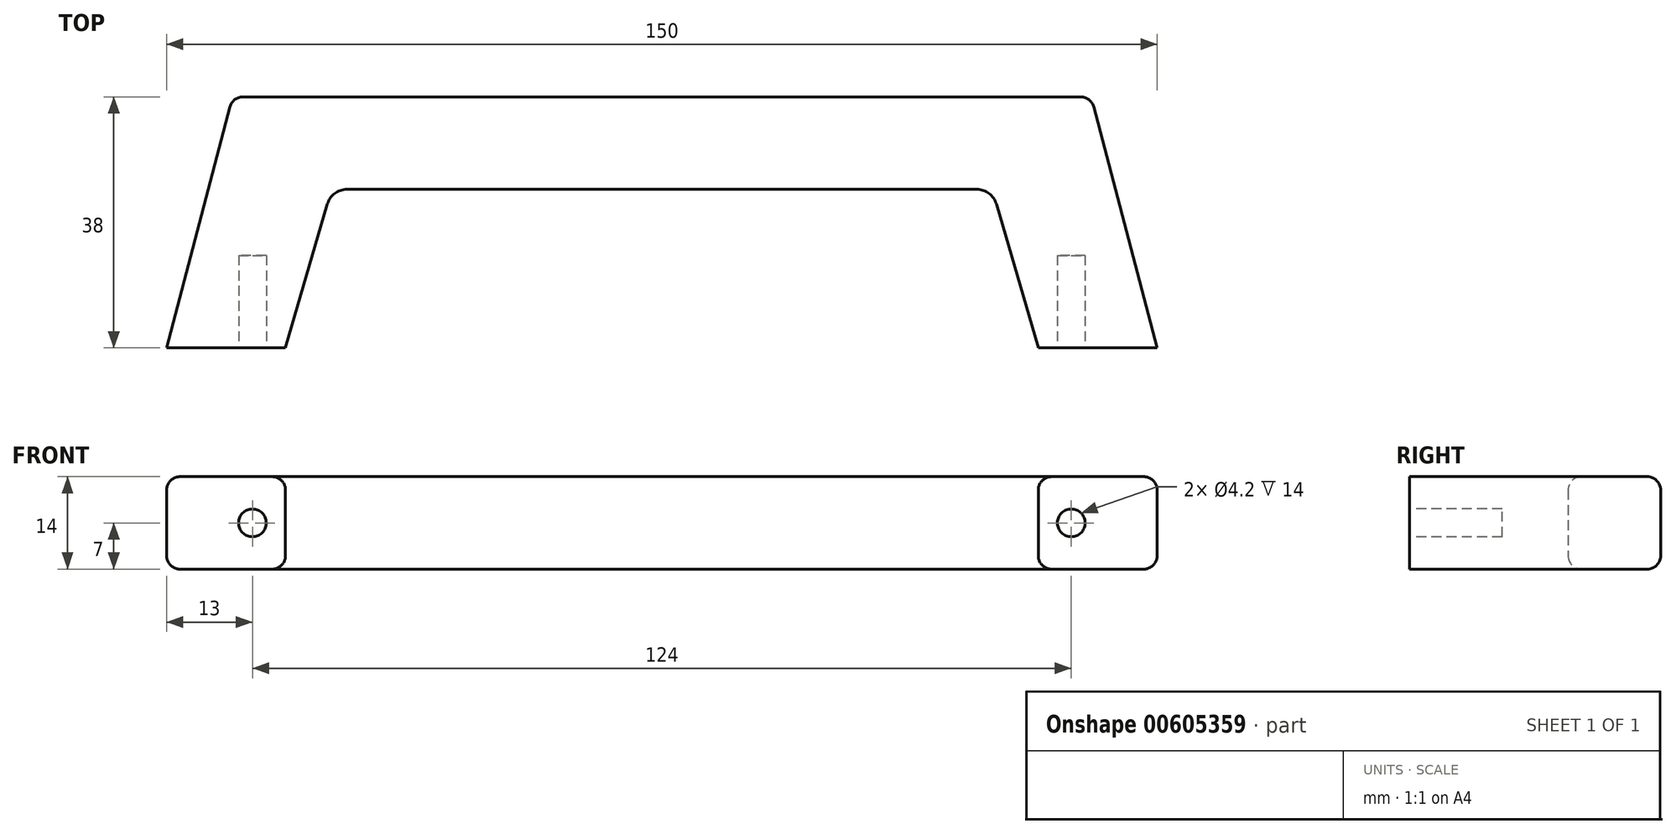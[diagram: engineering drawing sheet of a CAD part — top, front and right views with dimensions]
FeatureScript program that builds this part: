
annotation { "Feature Type Name" : "Feature", "Feature Type Description" : "" }
export const myFeature = defineFeature(function(context is Context, id is Id, definition is map)
    precondition{}
    {
        {
            var Q0;
            Q0=qCreatedBy(makeId("Top.planeOp"),FACE);
            var sketch = newSketch(context, id + "F0", { "sketchPlane" : qUnion([Q0])});
            skPoint(sketch, "E0.middle", {"position": v(0, 0) * mm});
            skLineSegment(sketch, "E1", {"start": v(-75, -19.5) * mm, "end": v(-65, 18.5) * mm});
            skLineSegment(sketch, "E2", {"start": v(-65, 18.5) * mm, "end": v(0, 18.5) * mm});
            skLineSegment(sketch, "E3", {"start": v(-75, -19.5) * mm, "end": v(-57, -19.5) * mm});
            skLineSegment(sketch, "E4", {"start": v(-50, 4.5) * mm, "end": v(0, 4.5) * mm});
            skLineSegment(sketch, "E5", {"start": v(-57, -19.5) * mm, "end": v(-50, 4.5) * mm});
            skPoint(sketch, "E6.orphan", {"position": v(0, 38.21) * mm});
            skPoint(sketch, "E0.right.end.orphan", {"position": v(75, -19.5) * mm});
            skPoint(sketch, "E0.right.start.orphan", {"position": v(75, 19.5) * mm});
            skLineSegment(sketch, "E7.MirrorCS", {"start": v(65, 18.5) * mm, "end": v(0, 18.5) * mm});
            skLineSegment(sketch, "E8.MirrorCS", {"start": v(50, 4.5) * mm, "end": v(0, 4.5) * mm});
            skLineSegment(sketch, "E9.MirrorCS", {"start": v(57, -19.5) * mm, "end": v(50, 4.5) * mm});
            skLineSegment(sketch, "E10.MirrorCS", {"start": v(75, -19.5) * mm, "end": v(65, 18.5) * mm});
            skLineSegment(sketch, "E11.MirrorCS", {"start": v(75, -19.5) * mm, "end": v(57, -19.5) * mm});
            skSolve(sketch);
        }
        {
            var Q0;
            Q0=makeQuery(id+"F0.imprint","IMPRINT",FACE,{"disambiguationData":[TD([[makeQuery(id+"F0.imprint","IMPRINT",EDGE,{"derivedFrom":sQuery(id+"F0.wireOp",EDGE,"E1")}),-1.0]])]});
            extrude(context, id + "F1", {"entities" : qUnion([Q0]), "depth" : 14 * mm, "offsetDistance" : 25 * mm});
        }
        {
            var Q0;
            Q0=makeQuery(id+"F1.opExtrude","SWEPT_FACE",FACE,{"disambiguationData":[OSD([sQuery(id+"F0.wireOp",EDGE,"E3")])]});
            var sketch = newSketch(context, id + "F2", { "sketchPlane" : qUnion([Q0])});
            skCircle(sketch, "E12", {"center": v(-62, 7) * mm, "radius": 2.1 * mm});
            skPoint(sketch, "E12.centerSnap0", {"position": v(-57, 7) * mm});
            skCircle(sketch, "E13.MirrorC", {"center": v(62, 7) * mm, "radius": 2.1 * mm});
            skSolve(sketch);
        }
        {
            var Q0;
            Q0 = qSketchRegion(id + "F2", true);
            extrude(context, id + "F3", {"entities" : qUnion([Q0]), "operationType" : NewBodyOperationType.REMOVE, "oppositeDirection" : true, "depth" : 14 * mm, "offsetDistance" : 25 * mm});
        }
        {
            var Q0;
            Q0=makeQuery(id+"F1.opExtrude","SWEPT_EDGE",EDGE,{"disambiguationData":[OSD([sQuery(id+"F0.wireOp",EDGE,"E7.MirrorCS"),sQuery(id+"F0.wireOp",EDGE,"E10.MirrorCS")])]});
            var Q1;
            Q1=makeQuery(id+"F1.opExtrude","SWEPT_EDGE",EDGE,{"disambiguationData":[OSD([sQuery(id+"F0.wireOp",EDGE,"E1"),sQuery(id+"F0.wireOp",EDGE,"E2")])]});
            fillet(context, id + "F4", {"entities" : qUnion([Q0, Q1]), "radius" : 2 * mm, "tangentPropagation" : true, "allowEdgeOverflow" : false});
        }
        {
            var Q0;
            Q0=makeQuery(id+"F1.opExtrude","SWEPT_EDGE",EDGE,{"disambiguationData":[OSD([sQuery(id+"F0.wireOp",EDGE,"E8.MirrorCS"),sQuery(id+"F0.wireOp",EDGE,"E9.MirrorCS")])]});
            var Q1;
            Q1=makeQuery(id+"F1.opExtrude","SWEPT_EDGE",EDGE,{"disambiguationData":[OSD([sQuery(id+"F0.wireOp",EDGE,"E4"),sQuery(id+"F0.wireOp",EDGE,"E5")])]});
            fillet(context, id + "F5", {"entities" : qUnion([Q0, Q1]), "radius" : 3.1 * mm, "tangentPropagation" : true, "allowEdgeOverflow" : false});
        }
        {
            var Q0;
            Q0=makeQuery(id+"F1.opExtrude","CAP_EDGE",EDGE,{"disambiguationData":[OSD([sQuery(id+"F0.wireOp",EDGE,"E2"),sQuery(id+"F0.wireOp",EDGE,"E7.MirrorCS")])],"isStart":true});
            var Q1;
            {var subQ0=sQuery(id+"F0.wireOp",EDGE,"E2");var subQ1=sQuery(id+"F0.wireOp",EDGE,"E1");Q1=makeQuery(id+"F4.opFillet","BLEND_EDGE",EDGE,{"blendedFrom":[makeQuery(id+"F1.opExtrude","SWEPT_EDGE",EDGE,{"disambiguationData":[OSD([subQ1,subQ0])]}),makeQuery(id+"F1.opExtrude","CAP_FACE",FACE,{"disambiguationData":[OSD([subQ1,subQ0,sQuery(id+"F0.wireOp",EDGE,"E3"),sQuery(id+"F0.wireOp",EDGE,"E4"),sQuery(id+"F0.wireOp",EDGE,"E5"),sQuery(id+"F0.wireOp",EDGE,"E7.MirrorCS"),sQuery(id+"F0.wireOp",EDGE,"E8.MirrorCS"),sQuery(id+"F0.wireOp",EDGE,"E9.MirrorCS"),sQuery(id+"F0.wireOp",EDGE,"E10.MirrorCS"),sQuery(id+"F0.wireOp",EDGE,"E11.MirrorCS")])],"isStart":true})],"blendedInto":[makeQuery(id+"F1.opExtrude","CAP_FACE",FACE,{"disambiguationData":[OSD([subQ1,subQ0,sQuery(id+"F0.wireOp",EDGE,"E3"),sQuery(id+"F0.wireOp",EDGE,"E4"),sQuery(id+"F0.wireOp",EDGE,"E5"),sQuery(id+"F0.wireOp",EDGE,"E7.MirrorCS"),sQuery(id+"F0.wireOp",EDGE,"E8.MirrorCS"),sQuery(id+"F0.wireOp",EDGE,"E9.MirrorCS"),sQuery(id+"F0.wireOp",EDGE,"E10.MirrorCS"),sQuery(id+"F0.wireOp",EDGE,"E11.MirrorCS")])],"isStart":true})]});}
            var Q2;
            Q2=makeQuery(id+"F1.opExtrude","CAP_EDGE",EDGE,{"disambiguationData":[OSD([sQuery(id+"F0.wireOp",EDGE,"E1")])],"isStart":true});
            var Q3;
            {var subQ0=sQuery(id+"F0.wireOp",EDGE,"E10.MirrorCS");var subQ1=sQuery(id+"F0.wireOp",EDGE,"E7.MirrorCS");Q3=makeQuery(id+"F4.opFillet","BLEND_EDGE",EDGE,{"blendedFrom":[makeQuery(id+"F1.opExtrude","SWEPT_EDGE",EDGE,{"disambiguationData":[OSD([subQ1,subQ0])]}),makeQuery(id+"F1.opExtrude","CAP_FACE",FACE,{"disambiguationData":[OSD([sQuery(id+"F0.wireOp",EDGE,"E1"),sQuery(id+"F0.wireOp",EDGE,"E2"),sQuery(id+"F0.wireOp",EDGE,"E3"),sQuery(id+"F0.wireOp",EDGE,"E4"),sQuery(id+"F0.wireOp",EDGE,"E5"),subQ1,sQuery(id+"F0.wireOp",EDGE,"E8.MirrorCS"),sQuery(id+"F0.wireOp",EDGE,"E9.MirrorCS"),subQ0,sQuery(id+"F0.wireOp",EDGE,"E11.MirrorCS")])],"isStart":true})],"blendedInto":[makeQuery(id+"F1.opExtrude","CAP_FACE",FACE,{"disambiguationData":[OSD([sQuery(id+"F0.wireOp",EDGE,"E1"),sQuery(id+"F0.wireOp",EDGE,"E2"),sQuery(id+"F0.wireOp",EDGE,"E3"),sQuery(id+"F0.wireOp",EDGE,"E4"),sQuery(id+"F0.wireOp",EDGE,"E5"),subQ1,sQuery(id+"F0.wireOp",EDGE,"E8.MirrorCS"),sQuery(id+"F0.wireOp",EDGE,"E9.MirrorCS"),subQ0,sQuery(id+"F0.wireOp",EDGE,"E11.MirrorCS")])],"isStart":true})]});}
            var Q4;
            Q4=makeQuery(id+"F1.opExtrude","CAP_EDGE",EDGE,{"disambiguationData":[OSD([sQuery(id+"F0.wireOp",EDGE,"E10.MirrorCS")])],"isStart":true});
            var Q5;
            Q5=makeQuery(id+"F1.opExtrude","CAP_EDGE",EDGE,{"disambiguationData":[OSD([sQuery(id+"F0.wireOp",EDGE,"E9.MirrorCS")])],"isStart":true});
            var Q6;
            {var subQ0=sQuery(id+"F0.wireOp",EDGE,"E9.MirrorCS");var subQ1=sQuery(id+"F0.wireOp",EDGE,"E8.MirrorCS");Q6=makeQuery(id+"F5.opFillet","BLEND_EDGE",EDGE,{"blendedFrom":[makeQuery(id+"F1.opExtrude","SWEPT_EDGE",EDGE,{"disambiguationData":[OSD([subQ1,subQ0])]}),makeQuery(id+"F1.opExtrude","CAP_FACE",FACE,{"disambiguationData":[OSD([sQuery(id+"F0.wireOp",EDGE,"E1"),sQuery(id+"F0.wireOp",EDGE,"E2"),sQuery(id+"F0.wireOp",EDGE,"E3"),sQuery(id+"F0.wireOp",EDGE,"E4"),sQuery(id+"F0.wireOp",EDGE,"E5"),sQuery(id+"F0.wireOp",EDGE,"E7.MirrorCS"),subQ1,subQ0,sQuery(id+"F0.wireOp",EDGE,"E10.MirrorCS"),sQuery(id+"F0.wireOp",EDGE,"E11.MirrorCS")])],"isStart":true})],"blendedInto":[makeQuery(id+"F1.opExtrude","CAP_FACE",FACE,{"disambiguationData":[OSD([sQuery(id+"F0.wireOp",EDGE,"E1"),sQuery(id+"F0.wireOp",EDGE,"E2"),sQuery(id+"F0.wireOp",EDGE,"E3"),sQuery(id+"F0.wireOp",EDGE,"E4"),sQuery(id+"F0.wireOp",EDGE,"E5"),sQuery(id+"F0.wireOp",EDGE,"E7.MirrorCS"),subQ1,subQ0,sQuery(id+"F0.wireOp",EDGE,"E10.MirrorCS"),sQuery(id+"F0.wireOp",EDGE,"E11.MirrorCS")])],"isStart":true})]});}
            var Q7;
            Q7=makeQuery(id+"F1.opExtrude","CAP_EDGE",EDGE,{"disambiguationData":[OSD([sQuery(id+"F0.wireOp",EDGE,"E4"),sQuery(id+"F0.wireOp",EDGE,"E8.MirrorCS")])],"isStart":true});
            var Q8;
            {var subQ0=sQuery(id+"F0.wireOp",EDGE,"E5");var subQ1=sQuery(id+"F0.wireOp",EDGE,"E4");Q8=makeQuery(id+"F5.opFillet","BLEND_EDGE",EDGE,{"blendedFrom":[makeQuery(id+"F1.opExtrude","SWEPT_EDGE",EDGE,{"disambiguationData":[OSD([subQ1,subQ0])]}),makeQuery(id+"F1.opExtrude","CAP_FACE",FACE,{"disambiguationData":[OSD([sQuery(id+"F0.wireOp",EDGE,"E1"),sQuery(id+"F0.wireOp",EDGE,"E2"),sQuery(id+"F0.wireOp",EDGE,"E3"),subQ1,subQ0,sQuery(id+"F0.wireOp",EDGE,"E7.MirrorCS"),sQuery(id+"F0.wireOp",EDGE,"E8.MirrorCS"),sQuery(id+"F0.wireOp",EDGE,"E9.MirrorCS"),sQuery(id+"F0.wireOp",EDGE,"E10.MirrorCS"),sQuery(id+"F0.wireOp",EDGE,"E11.MirrorCS")])],"isStart":true})],"blendedInto":[makeQuery(id+"F1.opExtrude","CAP_FACE",FACE,{"disambiguationData":[OSD([sQuery(id+"F0.wireOp",EDGE,"E1"),sQuery(id+"F0.wireOp",EDGE,"E2"),sQuery(id+"F0.wireOp",EDGE,"E3"),subQ1,subQ0,sQuery(id+"F0.wireOp",EDGE,"E7.MirrorCS"),sQuery(id+"F0.wireOp",EDGE,"E8.MirrorCS"),sQuery(id+"F0.wireOp",EDGE,"E9.MirrorCS"),sQuery(id+"F0.wireOp",EDGE,"E10.MirrorCS"),sQuery(id+"F0.wireOp",EDGE,"E11.MirrorCS")])],"isStart":true})]});}
            var Q9;
            Q9=makeQuery(id+"F1.opExtrude","CAP_EDGE",EDGE,{"disambiguationData":[OSD([sQuery(id+"F0.wireOp",EDGE,"E5")])],"isStart":true});
            var Q10;
            Q10=makeQuery(id+"F1.opExtrude","CAP_EDGE",EDGE,{"disambiguationData":[OSD([sQuery(id+"F0.wireOp",EDGE,"E1")])],"isStart":false});
            var Q11;
            {var subQ0=sQuery(id+"F0.wireOp",EDGE,"E2");var subQ1=sQuery(id+"F0.wireOp",EDGE,"E1");Q11=makeQuery(id+"F4.opFillet","BLEND_EDGE",EDGE,{"blendedFrom":[makeQuery(id+"F1.opExtrude","SWEPT_EDGE",EDGE,{"disambiguationData":[OSD([subQ1,subQ0])]}),makeQuery(id+"F1.opExtrude","CAP_FACE",FACE,{"disambiguationData":[OSD([subQ1,subQ0,sQuery(id+"F0.wireOp",EDGE,"E3"),sQuery(id+"F0.wireOp",EDGE,"E4"),sQuery(id+"F0.wireOp",EDGE,"E5"),sQuery(id+"F0.wireOp",EDGE,"E7.MirrorCS"),sQuery(id+"F0.wireOp",EDGE,"E8.MirrorCS"),sQuery(id+"F0.wireOp",EDGE,"E9.MirrorCS"),sQuery(id+"F0.wireOp",EDGE,"E10.MirrorCS"),sQuery(id+"F0.wireOp",EDGE,"E11.MirrorCS")])],"isStart":false})],"blendedInto":[makeQuery(id+"F1.opExtrude","CAP_FACE",FACE,{"disambiguationData":[OSD([subQ1,subQ0,sQuery(id+"F0.wireOp",EDGE,"E3"),sQuery(id+"F0.wireOp",EDGE,"E4"),sQuery(id+"F0.wireOp",EDGE,"E5"),sQuery(id+"F0.wireOp",EDGE,"E7.MirrorCS"),sQuery(id+"F0.wireOp",EDGE,"E8.MirrorCS"),sQuery(id+"F0.wireOp",EDGE,"E9.MirrorCS"),sQuery(id+"F0.wireOp",EDGE,"E10.MirrorCS"),sQuery(id+"F0.wireOp",EDGE,"E11.MirrorCS")])],"isStart":false})]});}
            var Q12;
            Q12=makeQuery(id+"F1.opExtrude","CAP_EDGE",EDGE,{"disambiguationData":[OSD([sQuery(id+"F0.wireOp",EDGE,"E2"),sQuery(id+"F0.wireOp",EDGE,"E7.MirrorCS")])],"isStart":false});
            var Q13;
            {var subQ0=sQuery(id+"F0.wireOp",EDGE,"E10.MirrorCS");var subQ1=sQuery(id+"F0.wireOp",EDGE,"E7.MirrorCS");Q13=makeQuery(id+"F4.opFillet","BLEND_EDGE",EDGE,{"blendedFrom":[makeQuery(id+"F1.opExtrude","SWEPT_EDGE",EDGE,{"disambiguationData":[OSD([subQ1,subQ0])]}),makeQuery(id+"F1.opExtrude","CAP_FACE",FACE,{"disambiguationData":[OSD([sQuery(id+"F0.wireOp",EDGE,"E1"),sQuery(id+"F0.wireOp",EDGE,"E2"),sQuery(id+"F0.wireOp",EDGE,"E3"),sQuery(id+"F0.wireOp",EDGE,"E4"),sQuery(id+"F0.wireOp",EDGE,"E5"),subQ1,sQuery(id+"F0.wireOp",EDGE,"E8.MirrorCS"),sQuery(id+"F0.wireOp",EDGE,"E9.MirrorCS"),subQ0,sQuery(id+"F0.wireOp",EDGE,"E11.MirrorCS")])],"isStart":false})],"blendedInto":[makeQuery(id+"F1.opExtrude","CAP_FACE",FACE,{"disambiguationData":[OSD([sQuery(id+"F0.wireOp",EDGE,"E1"),sQuery(id+"F0.wireOp",EDGE,"E2"),sQuery(id+"F0.wireOp",EDGE,"E3"),sQuery(id+"F0.wireOp",EDGE,"E4"),sQuery(id+"F0.wireOp",EDGE,"E5"),subQ1,sQuery(id+"F0.wireOp",EDGE,"E8.MirrorCS"),sQuery(id+"F0.wireOp",EDGE,"E9.MirrorCS"),subQ0,sQuery(id+"F0.wireOp",EDGE,"E11.MirrorCS")])],"isStart":false})]});}
            var Q14;
            Q14=makeQuery(id+"F1.opExtrude","CAP_EDGE",EDGE,{"disambiguationData":[OSD([sQuery(id+"F0.wireOp",EDGE,"E10.MirrorCS")])],"isStart":false});
            var Q15;
            {var subQ0=sQuery(id+"F0.wireOp",EDGE,"E9.MirrorCS");var subQ1=sQuery(id+"F0.wireOp",EDGE,"E8.MirrorCS");Q15=makeQuery(id+"F5.opFillet","BLEND_EDGE",EDGE,{"blendedFrom":[makeQuery(id+"F1.opExtrude","SWEPT_EDGE",EDGE,{"disambiguationData":[OSD([subQ1,subQ0])]}),makeQuery(id+"F1.opExtrude","CAP_FACE",FACE,{"disambiguationData":[OSD([sQuery(id+"F0.wireOp",EDGE,"E1"),sQuery(id+"F0.wireOp",EDGE,"E2"),sQuery(id+"F0.wireOp",EDGE,"E3"),sQuery(id+"F0.wireOp",EDGE,"E4"),sQuery(id+"F0.wireOp",EDGE,"E5"),sQuery(id+"F0.wireOp",EDGE,"E7.MirrorCS"),subQ1,subQ0,sQuery(id+"F0.wireOp",EDGE,"E10.MirrorCS"),sQuery(id+"F0.wireOp",EDGE,"E11.MirrorCS")])],"isStart":false})],"blendedInto":[makeQuery(id+"F1.opExtrude","CAP_FACE",FACE,{"disambiguationData":[OSD([sQuery(id+"F0.wireOp",EDGE,"E1"),sQuery(id+"F0.wireOp",EDGE,"E2"),sQuery(id+"F0.wireOp",EDGE,"E3"),sQuery(id+"F0.wireOp",EDGE,"E4"),sQuery(id+"F0.wireOp",EDGE,"E5"),sQuery(id+"F0.wireOp",EDGE,"E7.MirrorCS"),subQ1,subQ0,sQuery(id+"F0.wireOp",EDGE,"E10.MirrorCS"),sQuery(id+"F0.wireOp",EDGE,"E11.MirrorCS")])],"isStart":false})]});}
            var Q16;
            Q16=makeQuery(id+"F1.opExtrude","CAP_EDGE",EDGE,{"disambiguationData":[OSD([sQuery(id+"F0.wireOp",EDGE,"E4"),sQuery(id+"F0.wireOp",EDGE,"E8.MirrorCS")])],"isStart":false});
            var Q17;
            Q17=makeQuery(id+"F1.opExtrude","CAP_EDGE",EDGE,{"disambiguationData":[OSD([sQuery(id+"F0.wireOp",EDGE,"E9.MirrorCS")])],"isStart":false});
            var Q18;
            {var subQ0=sQuery(id+"F0.wireOp",EDGE,"E5");var subQ1=sQuery(id+"F0.wireOp",EDGE,"E4");Q18=makeQuery(id+"F5.opFillet","BLEND_EDGE",EDGE,{"blendedFrom":[makeQuery(id+"F1.opExtrude","SWEPT_EDGE",EDGE,{"disambiguationData":[OSD([subQ1,subQ0])]}),makeQuery(id+"F1.opExtrude","CAP_FACE",FACE,{"disambiguationData":[OSD([sQuery(id+"F0.wireOp",EDGE,"E1"),sQuery(id+"F0.wireOp",EDGE,"E2"),sQuery(id+"F0.wireOp",EDGE,"E3"),subQ1,subQ0,sQuery(id+"F0.wireOp",EDGE,"E7.MirrorCS"),sQuery(id+"F0.wireOp",EDGE,"E8.MirrorCS"),sQuery(id+"F0.wireOp",EDGE,"E9.MirrorCS"),sQuery(id+"F0.wireOp",EDGE,"E10.MirrorCS"),sQuery(id+"F0.wireOp",EDGE,"E11.MirrorCS")])],"isStart":false})],"blendedInto":[makeQuery(id+"F1.opExtrude","CAP_FACE",FACE,{"disambiguationData":[OSD([sQuery(id+"F0.wireOp",EDGE,"E1"),sQuery(id+"F0.wireOp",EDGE,"E2"),sQuery(id+"F0.wireOp",EDGE,"E3"),subQ1,subQ0,sQuery(id+"F0.wireOp",EDGE,"E7.MirrorCS"),sQuery(id+"F0.wireOp",EDGE,"E8.MirrorCS"),sQuery(id+"F0.wireOp",EDGE,"E9.MirrorCS"),sQuery(id+"F0.wireOp",EDGE,"E10.MirrorCS"),sQuery(id+"F0.wireOp",EDGE,"E11.MirrorCS")])],"isStart":false})]});}
            var Q19;
            Q19=makeQuery(id+"F1.opExtrude","CAP_EDGE",EDGE,{"disambiguationData":[OSD([sQuery(id+"F0.wireOp",EDGE,"E5")])],"isStart":false});
            fillet(context, id + "F6", {"entities" : qUnion([Q0, Q1, Q2, Q3, Q4, Q5, Q6, Q7, Q8, Q9, Q10, Q11, Q12, Q13, Q14, Q15, Q16, Q17, Q18, Q19]), "radius" : 2 * mm, "tangentPropagation" : true, "allowEdgeOverflow" : false});
        }
    });
